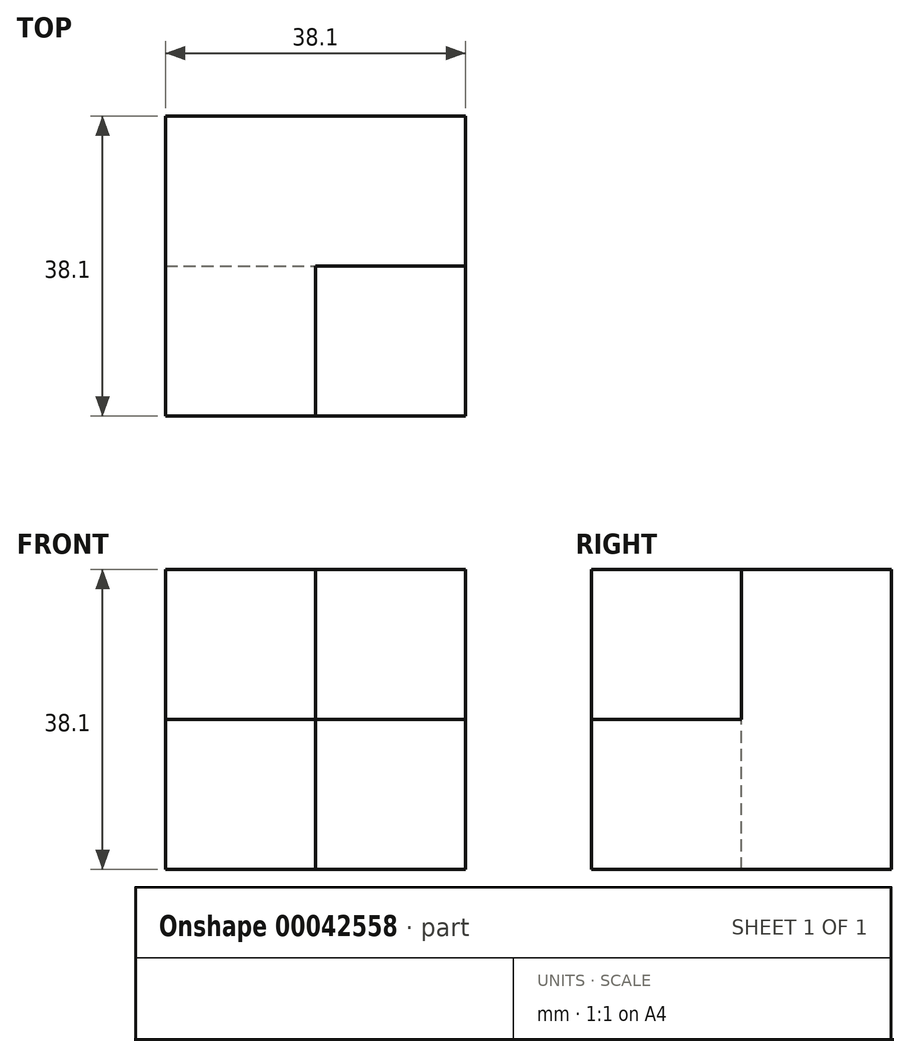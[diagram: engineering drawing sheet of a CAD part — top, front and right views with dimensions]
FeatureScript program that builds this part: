
annotation { "Feature Type Name" : "Feature", "Feature Type Description" : "" }
export const myFeature = defineFeature(function(context is Context, id is Id, definition is map)
    precondition{}
    {
        {
            var Q0;
            Q0=qCreatedBy(makeId("Front.planeOp"),FACE);
            var sketch = newSketch(context, id + "F0", { "sketchPlane" : qUnion([Q0])});
            skLineSegment(sketch, "E0.bottom", {"start": v(0, 0) * mm, "end": v(38.1, 0) * mm});
            skLineSegment(sketch, "E0.top", {"start": v(0, 38.1) * mm, "end": v(38.1, 38.1) * mm});
            skLineSegment(sketch, "E0.left", {"start": v(0, 0) * mm, "end": v(0, 38.1) * mm});
            skLineSegment(sketch, "E0.right", {"start": v(38.1, 0) * mm, "end": v(38.1, 38.1) * mm});
            skSolve(sketch);
        }
        {
            var Q0;
            Q0=makeQuery(id+"F0.imprint","IMPRINT",FACE,{"disambiguationData":[TD([[makeQuery(id+"F0.imprint","IMPRINT",EDGE,{"derivedFrom":sQuery(id+"F0.wireOp",EDGE,"E0.bottom")}),1.0]])]});
            extrude(context, id + "F1", {"entities" : qUnion([Q0]), "depth" : 19.05 * mm});
        }
        {
            var Q0;
            Q0=makeQuery(id+"F1.opExtrude","CAP_FACE",FACE,{"disambiguationData":[OSD([sQuery(id+"F0.wireOp",EDGE,"E0.bottom"),sQuery(id+"F0.wireOp",EDGE,"E0.top"),sQuery(id+"F0.wireOp",EDGE,"E0.left"),sQuery(id+"F0.wireOp",EDGE,"E0.right")])],"isStart":false});
            var sketch = newSketch(context, id + "F2", { "sketchPlane" : qUnion([Q0])});
            skLineSegment(sketch, "E1.bottom", {"start": v(0, 38.1) * mm, "end": v(19.05, 38.1) * mm});
            skLineSegment(sketch, "E1.top", {"start": v(0, 19.05) * mm, "end": v(19.05, 19.05) * mm});
            skLineSegment(sketch, "E1.left", {"start": v(0, 38.1) * mm, "end": v(0, 19.05) * mm});
            skLineSegment(sketch, "E1.right", {"start": v(19.05, 38.1) * mm, "end": v(19.05, 19.05) * mm});
            skSolve(sketch);
        }
        {
            var Q0;
            Q0=qSketchRegion(id+"F2",true);
            extrude(context, id + "F3", {"entities" : qUnion([Q0]), "operationType" : NewBodyOperationType.ADD, "depth" : 19.05 * mm});
        }
        {
            var Q0;
            Q0=makeQuery(id+"F1.opExtrude","CAP_FACE",FACE,{"disambiguationData":[OSD([sQuery(id+"F0.wireOp",EDGE,"E0.bottom"),sQuery(id+"F0.wireOp",EDGE,"E0.top"),sQuery(id+"F0.wireOp",EDGE,"E0.left"),sQuery(id+"F0.wireOp",EDGE,"E0.right")])],"isStart":false});
            var sketch = newSketch(context, id + "F4", { "sketchPlane" : qUnion([Q0])});
            skLineSegment(sketch, "E2.bottom", {"start": v(38.1, 0) * mm, "end": v(19.05, 0) * mm});
            skLineSegment(sketch, "E2.top", {"start": v(38.1, 19.05) * mm, "end": v(19.05, 19.05) * mm});
            skLineSegment(sketch, "E2.left", {"start": v(38.1, 0) * mm, "end": v(38.1, 19.05) * mm});
            skLineSegment(sketch, "E2.right", {"start": v(19.05, 0) * mm, "end": v(19.05, 19.05) * mm});
            skSolve(sketch);
        }
        {
            var Q0;
            Q0=makeQuery(id+"F3.opExtrude","SWEPT_EDGE",EDGE,{"disambiguationData":[OSD([sQuery(id+"F2.wireOp",EDGE,"E1.top"),sQuery(id+"F2.wireOp",EDGE,"E1.right")])]});
            chamfer(context, id + "F5", {"entities" : qUnion([Q0]), "width" : 0.03 * mm, "tangentPropagation" : true});
        }
        {
            var Q0;
            Q0=qSketchRegion(id+"F4",true);
            extrude(context, id + "F6", {"entities" : qUnion([Q0]), "operationType" : NewBodyOperationType.ADD, "depth" : 19.05 * mm});
        }
    });
